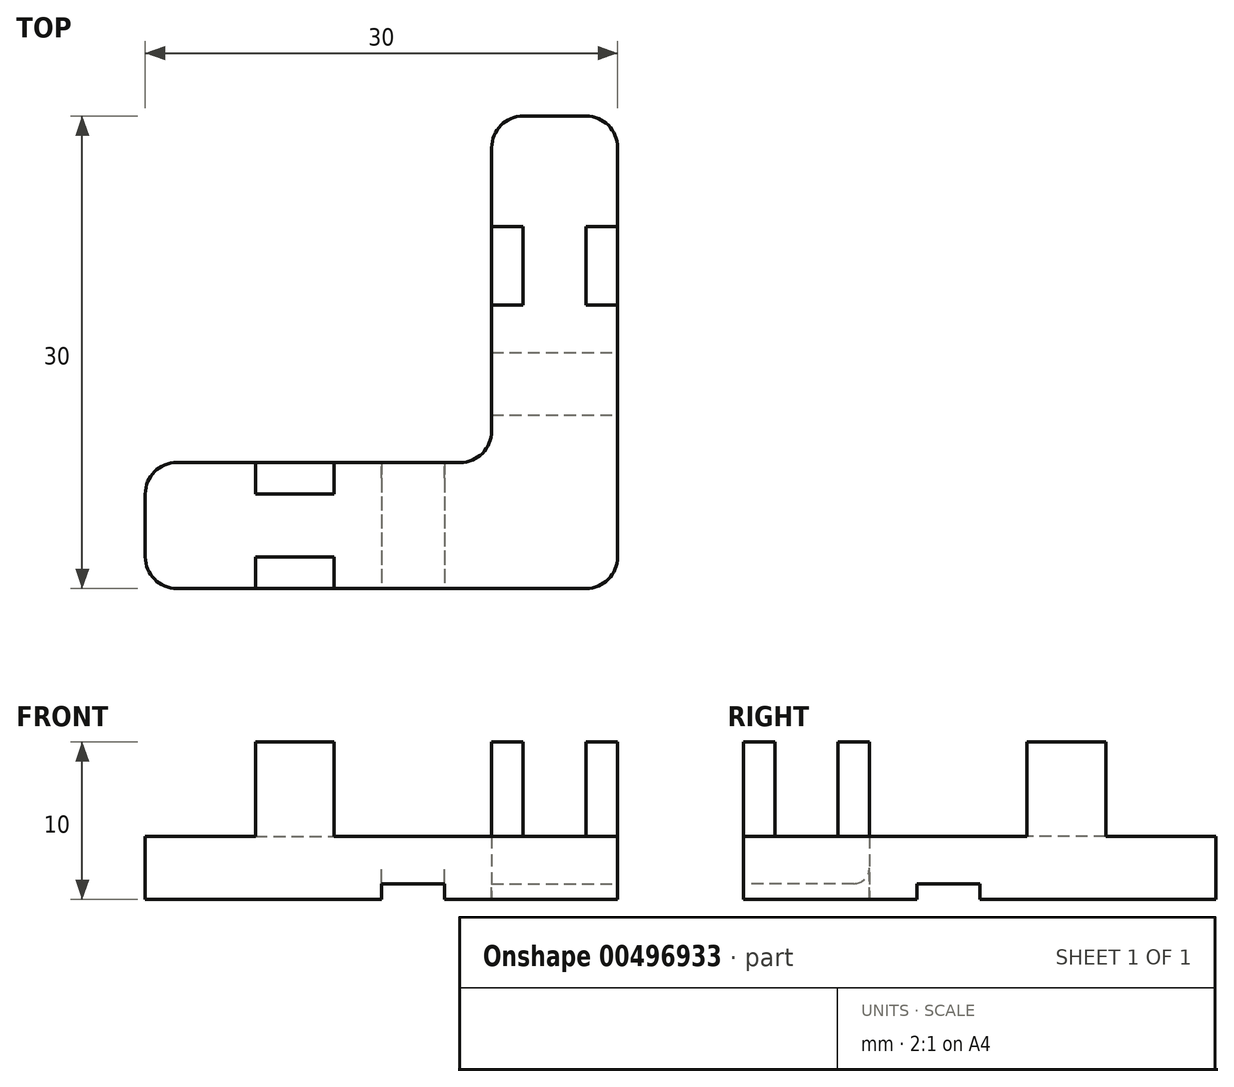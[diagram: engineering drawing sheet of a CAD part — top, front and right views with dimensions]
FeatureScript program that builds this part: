
annotation { "Feature Type Name" : "Feature", "Feature Type Description" : "" }
export const myFeature = defineFeature(function(context is Context, id is Id, definition is map)
    precondition{}
    {
        {
            var Q0;
            Q0=qCreatedBy(makeId("Top.planeOp"),FACE);
            var sketch = newSketch(context, id + "F0", { "sketchPlane" : qUnion([Q0])});
            skLineSegment(sketch, "E0", {"start": v(8, 22) * mm, "end": v(8, -8) * mm});
            skLineSegment(sketch, "E1", {"start": v(8, -8) * mm, "end": v(-22, -8) * mm});
            skLineSegment(sketch, "E2.0", {"start": v(0, 0) * mm, "end": v(-22, 0) * mm});
            skLineSegment(sketch, "E2.1", {"start": v(0, 22) * mm, "end": v(0, 0) * mm});
            skLineSegment(sketch, "E3", {"start": v(0, 22) * mm, "end": v(8, 22) * mm});
            skLineSegment(sketch, "E4", {"start": v(-22, 0) * mm, "end": v(-22, -8) * mm});
            skSolve(sketch);
        }
        {
            var Q0;
            Q0=makeQuery(id+"F0.imprint","IMPRINT",FACE,{"disambiguationData":[TD([[makeQuery(id+"F0.imprint","IMPRINT",EDGE,{"derivedFrom":sQuery(id+"F0.wireOp",EDGE,"E0")}),-1.0]])]});
            extrude(context, id + "F1", {"entities" : qUnion([Q0]), "depth" : 4 * mm});
        }
        {
            var Q0;
            Q0=makeQuery(id+"F1.opExtrude","CAP_FACE",FACE,{"disambiguationData":[OSD([sQuery(id+"F0.wireOp",EDGE,"E0"),sQuery(id+"F0.wireOp",EDGE,"E1"),sQuery(id+"F0.wireOp",EDGE,"E2.0"),sQuery(id+"F0.wireOp",EDGE,"E2.1"),sQuery(id+"F0.wireOp",EDGE,"E3"),sQuery(id+"F0.wireOp",EDGE,"E4")])],"isStart":false});
            var sketch = newSketch(context, id + "F2", { "sketchPlane" : qUnion([Q0])});
            skLineSegment(sketch, "E5.bottom", {"start": v(0, 15) * mm, "end": v(2, 15) * mm});
            skLineSegment(sketch, "E5.top", {"start": v(0, 10) * mm, "end": v(2, 10) * mm});
            skLineSegment(sketch, "E5.left", {"start": v(0, 15) * mm, "end": v(0, 10) * mm});
            skLineSegment(sketch, "E5.right", {"start": v(2, 15) * mm, "end": v(2, 10) * mm});
            skLineSegment(sketch, "E6.bottom", {"start": v(8, 15) * mm, "end": v(6, 15) * mm});
            skLineSegment(sketch, "E6.top", {"start": v(8, 10) * mm, "end": v(6, 10) * mm});
            skLineSegment(sketch, "E6.left", {"start": v(8, 15) * mm, "end": v(8, 10) * mm});
            skLineSegment(sketch, "E6.right", {"start": v(6, 15) * mm, "end": v(6, 10) * mm});
            skLineSegment(sketch, "E7.bottom", {"start": v(-15, 0) * mm, "end": v(-10, 0) * mm});
            skLineSegment(sketch, "E7.top", {"start": v(-15, -2) * mm, "end": v(-10, -2) * mm});
            skLineSegment(sketch, "E7.left", {"start": v(-15, 0) * mm, "end": v(-15, -2) * mm});
            skLineSegment(sketch, "E7.right", {"start": v(-10, 0) * mm, "end": v(-10, -2) * mm});
            skLineSegment(sketch, "E8.bottom", {"start": v(-15, -8) * mm, "end": v(-10, -8) * mm});
            skLineSegment(sketch, "E8.top", {"start": v(-15, -6) * mm, "end": v(-10, -6) * mm});
            skLineSegment(sketch, "E8.left", {"start": v(-15, -8) * mm, "end": v(-15, -6) * mm});
            skLineSegment(sketch, "E8.right", {"start": v(-10, -8) * mm, "end": v(-10, -6) * mm});
            skSolve(sketch);
        }
        {
            var Q0;
            Q0=makeQuery(id+"F2.imprint","IMPRINT",FACE,{"disambiguationData":[TD([[makeQuery(id+"F2.imprint","IMPRINT",EDGE,{"derivedFrom":sQuery(id+"F2.wireOp",EDGE,"E5.bottom")}),-1.0]])]});
            var Q1;
            Q1=makeQuery(id+"F2.imprint","IMPRINT",FACE,{"disambiguationData":[TD([[makeQuery(id+"F2.imprint","IMPRINT",EDGE,{"derivedFrom":sQuery(id+"F2.wireOp",EDGE,"E6.bottom")}),1.0]])]});
            var Q2;
            Q2=makeQuery(id+"F2.imprint","IMPRINT",FACE,{"disambiguationData":[TD([[makeQuery(id+"F2.imprint","IMPRINT",EDGE,{"derivedFrom":sQuery(id+"F2.wireOp",EDGE,"E7.bottom")}),1.0]])]});
            var Q3;
            Q3=makeQuery(id+"F2.imprint","IMPRINT",FACE,{"disambiguationData":[TD([[makeQuery(id+"F2.imprint","IMPRINT",EDGE,{"derivedFrom":sQuery(id+"F2.wireOp",EDGE,"E8.bottom")}),-1.0]])]});
            extrude(context, id + "F3", {"entities" : qUnion([Q0, Q1, Q2, Q3]), "operationType" : NewBodyOperationType.ADD, "depth" : 6 * mm});
        }
        {
            var Q0;
            Q0=makeQuery(id+"F3.opExtrude","CAP_EDGE",EDGE,{"disambiguationData":[OSD([sQuery(id+"F2.wireOp",EDGE,"E5.bottom")])],"isStart":true});
            var Q1;
            Q1=makeQuery(id+"F3.opExtrude","CAP_EDGE",EDGE,{"disambiguationData":[OSD([sQuery(id+"F2.wireOp",EDGE,"E5.right")])],"isStart":true});
            var Q2;
            Q2=makeQuery(id+"F3.opExtrude","CAP_EDGE",EDGE,{"disambiguationData":[OSD([sQuery(id+"F2.wireOp",EDGE,"E6.bottom")])],"isStart":true});
            var Q3;
            Q3=makeQuery(id+"F3.opExtrude","CAP_EDGE",EDGE,{"disambiguationData":[OSD([sQuery(id+"F2.wireOp",EDGE,"E8.top")])],"isStart":true});
            var Q4;
            Q4=makeQuery(id+"F3.opExtrude","CAP_EDGE",EDGE,{"disambiguationData":[OSD([sQuery(id+"F2.wireOp",EDGE,"E8.right")])],"isStart":true});
            var Q5;
            Q5=makeQuery(id+"F3.opExtrude","CAP_EDGE",EDGE,{"disambiguationData":[OSD([sQuery(id+"F2.wireOp",EDGE,"E5.top")])],"isStart":true});
            var Q6;
            Q6=makeQuery(id+"F3.opExtrude","CAP_EDGE",EDGE,{"disambiguationData":[OSD([sQuery(id+"F2.wireOp",EDGE,"E6.top")])],"isStart":true});
            var Q7;
            Q7=makeQuery(id+"F3.opExtrude","CAP_EDGE",EDGE,{"disambiguationData":[OSD([sQuery(id+"F2.wireOp",EDGE,"E6.right")])],"isStart":true});
            var Q8;
            Q8=makeQuery(id+"F3.opExtrude","CAP_EDGE",EDGE,{"disambiguationData":[OSD([sQuery(id+"F2.wireOp",EDGE,"E8.left")])],"isStart":true});
            var Q9;
            Q9=makeQuery(id+"F1.opExtrude","SWEPT_EDGE",EDGE,{"disambiguationData":[OSD([sQuery(id+"F0.wireOp",EDGE,"E2.0"),sQuery(id+"F0.wireOp",EDGE,"E2.1")])]});
            var Q10;
            Q10=makeQuery(id+"F1.opExtrude","SWEPT_EDGE",EDGE,{"disambiguationData":[OSD([sQuery(id+"F0.wireOp",EDGE,"E0"),sQuery(id+"F0.wireOp",EDGE,"E1")])]});
            var Q11;
            Q11=makeQuery(id+"F3.opExtrude","CAP_EDGE",EDGE,{"disambiguationData":[OSD([sQuery(id+"F2.wireOp",EDGE,"E7.left")])],"isStart":true});
            var Q12;
            Q12=makeQuery(id+"F3.opExtrude","CAP_EDGE",EDGE,{"disambiguationData":[OSD([sQuery(id+"F2.wireOp",EDGE,"E7.top")])],"isStart":true});
            var Q13;
            Q13=makeQuery(id+"F3.opExtrude","CAP_EDGE",EDGE,{"disambiguationData":[OSD([sQuery(id+"F2.wireOp",EDGE,"E7.right")])],"isStart":true});
            var Q14;
            Q14=makeQuery(id+"F1.opExtrude","SWEPT_EDGE",EDGE,{"disambiguationData":[OSD([sQuery(id+"F0.wireOp",EDGE,"E0"),sQuery(id+"F0.wireOp",EDGE,"E3")])]});
            var Q15;
            Q15=makeQuery(id+"F1.opExtrude","SWEPT_EDGE",EDGE,{"disambiguationData":[OSD([sQuery(id+"F0.wireOp",EDGE,"E2.1"),sQuery(id+"F0.wireOp",EDGE,"E3")])]});
            var Q16;
            Q16=makeQuery(id+"F1.opExtrude","SWEPT_EDGE",EDGE,{"disambiguationData":[OSD([sQuery(id+"F0.wireOp",EDGE,"E1"),sQuery(id+"F0.wireOp",EDGE,"E4")])]});
            var Q17;
            Q17=makeQuery(id+"F1.opExtrude","SWEPT_EDGE",EDGE,{"disambiguationData":[OSD([sQuery(id+"F0.wireOp",EDGE,"E2.0"),sQuery(id+"F0.wireOp",EDGE,"E4")])]});
            fillet(context, id + "F4", {"entities" : qUnion([Q0, Q1, Q2, Q3, Q4, Q5, Q6, Q7, Q8, Q9, Q10, Q11, Q12, Q13, Q14, Q15, Q16, Q17]), "radius" : 2 * mm, "tangentPropagation" : true, "allowEdgeOverflow" : false});
        }
        {
            var Q0;
            Q0=makeQuery(id+"F3.boolean.opBoolean","MERGE",FACE,{"derivedFrom":[makeQuery(id+"F1.opExtrude","SWEPT_FACE",FACE,{"disambiguationData":[OSD([sQuery(id+"F0.wireOp",EDGE,"E1")])]}),makeQuery(id+"F3.opExtrude","SWEPT_FACE",FACE,{"disambiguationData":[OSD([sQuery(id+"F2.wireOp",EDGE,"E8.bottom")])]})]});
            var sketch = newSketch(context, id + "F5", { "sketchPlane" : qUnion([Q0])});
            skLineSegment(sketch, "E9.bottom", {"start": v(-7, 0) * mm, "end": v(-3, 0) * mm});
            skLineSegment(sketch, "E9.top", {"start": v(-7, 1) * mm, "end": v(-3, 1) * mm});
            skLineSegment(sketch, "E9.left", {"start": v(-7, 0) * mm, "end": v(-7, 1) * mm});
            skLineSegment(sketch, "E9.right", {"start": v(-3, 0) * mm, "end": v(-3, 1) * mm});
            skSolve(sketch);
        }
        {
            var Q0;
            Q0=makeQuery(id+"F5.imprint","IMPRINT",FACE,{"disambiguationData":[TD([[makeQuery(id+"F5.imprint","IMPRINT",EDGE,{"derivedFrom":sQuery(id+"F5.wireOp",EDGE,"E9.bottom")}),-1.0]])]});
            extrude(context, id + "F6", {"entities" : qUnion([Q0]), "operationType" : NewBodyOperationType.REMOVE, "oppositeDirection" : true, "depth" : 25 * mm});
        }
        {
            var Q0;
            Q0=makeQuery(id+"F6.boolean.opBoolean","COPY",EDGE,{"derivedFrom":makeQuery(id+"F6.opExtrude","CAP_EDGE",EDGE,{"disambiguationData":[OSD([sQuery(id+"F5.wireOp",EDGE,"E9.top")])],"isStart":true})});
            var Q1;
            Q1=makeQuery(id+"F6.boolean.opBoolean","INTERSECT",EDGE,{"derivedFrom":[makeQuery(id+"F3.boolean.opBoolean","MERGE",FACE,{"derivedFrom":[makeQuery(id+"F1.opExtrude","SWEPT_FACE",FACE,{"disambiguationData":[OSD([sQuery(id+"F0.wireOp",EDGE,"E2.0")])]}),makeQuery(id+"F3.opExtrude","SWEPT_FACE",FACE,{"disambiguationData":[OSD([sQuery(id+"F2.wireOp",EDGE,"E7.bottom")])]})]}),makeQuery(id+"F6.opExtrude","SWEPT_FACE",FACE,{"disambiguationData":[OSD([sQuery(id+"F5.wireOp",EDGE,"E9.top")])]})]});
            fillet(context, id + "F7", {"entities" : qUnion([Q0, Q1]), "radius" : 1 * mm, "tangentPropagation" : true, "allowEdgeOverflow" : false});
        }
        {
            var Q0;
            Q0=makeQuery(id+"F3.boolean.opBoolean","MERGE",FACE,{"derivedFrom":[makeQuery(id+"F1.opExtrude","SWEPT_FACE",FACE,{"disambiguationData":[OSD([sQuery(id+"F0.wireOp",EDGE,"E0")])]}),makeQuery(id+"F3.opExtrude","SWEPT_FACE",FACE,{"disambiguationData":[OSD([sQuery(id+"F2.wireOp",EDGE,"E6.left")])]})]});
            var sketch = newSketch(context, id + "F8", { "sketchPlane" : qUnion([Q0])});
            skLineSegment(sketch, "E10.bottom", {"start": v(3, 0) * mm, "end": v(7, 0) * mm});
            skLineSegment(sketch, "E10.top", {"start": v(3, 1) * mm, "end": v(7, 1) * mm});
            skLineSegment(sketch, "E10.left", {"start": v(3, 0) * mm, "end": v(3, 1) * mm});
            skLineSegment(sketch, "E10.right", {"start": v(7, 0) * mm, "end": v(7, 1) * mm});
            skSolve(sketch);
        }
        {
            var Q0;
            Q0=makeQuery(id+"F8.imprint","IMPRINT",FACE,{"disambiguationData":[TD([[makeQuery(id+"F8.imprint","IMPRINT",EDGE,{"derivedFrom":sQuery(id+"F8.wireOp",EDGE,"E10.bottom")}),-1.0]])]});
            extrude(context, id + "F9", {"entities" : qUnion([Q0]), "operationType" : NewBodyOperationType.REMOVE, "oppositeDirection" : true, "depth" : 25 * mm});
        }
    });
